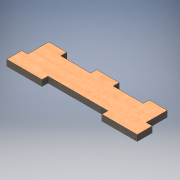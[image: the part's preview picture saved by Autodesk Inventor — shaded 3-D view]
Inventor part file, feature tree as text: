
AUTODESK INVENTOR PART (.ipt)
format: ipt  version: 2019 (Build 230136000, 136)  size: 159,744 bytes
history: native  units: mm
features: other x1, extrude x1, sketch x1
ambient origin geometry x8: Origin, YZ Plane, XZ Plane, XY Plane, X Axis, Y Axis, Z Axis, Center Point
bodies: Body1 (feature_tree)
feature tree (3):
  other  "Твердое тело1"
  extrude  "Выдавливание1"  Depth=12.0mm
  sketch  "Эскиз1"
